# Revit family: Sink-Top_Undermount-Kitchen-KOHLER-Vault-K-80169_1
name_source: partatom
category: Plumbing Fixtures
units: mm (PartAtom-declared; Revit-internal decimal feet)

## family parameters
Cut with Voids When Loaded = No
Host = Face
OmniClass Number = 23.31.13.00
OmniClass Title = Sinks
Part Type = Normal
Room Calculation Point = No
Round Connector Dimension = Use Diameter
Shared = No

## types (2) — shared parameters
ADA Compliant = No
Assembly Code = D2010400
CW Connection = No
Cold Water Inlet = Cold Water Inlet
Date Modified = 04/07/2023
Default Elevation = 36"
Description = 30.5 inch Large Single Sink, One Hole
Drain Included = Yes
HW Connection = No
Height = 11 11/16"
Hot Water Inlet = Hot Water Inlet
Length = 30 1/2"
Manufacturer = Kohler Co.
Master Format 2014 = 22 41 16
Master Format 2014 Name = Residential Lavatories and Sinks
Material = Stainless Steel
Product Documentation Link = https://www.us.kohler.com
Product Name = Vault
Product Page URL = http://www.us.kohler.com
URL = https://www.us.kohler.com
Vent Connection = No
Waste Connection = Yes
Waste Water Outlet = Waste Water Outlet
WaterSense Certified = No
Width = 20"

## per-type parameters (varying)
| type | Finish | Model | Type |
| ST-Stainless Steel | KOHLER-Metal-ST-Stainless_Steel | K-80169-1-ST | 1 |
| NA-Stainless | Kohler-Metal-NA-Stainless | K-80169-1-NA | 2 |

## geometry (parser evidence)
native form markers: Sweep x5
no freeform markers — native parametric forms only
